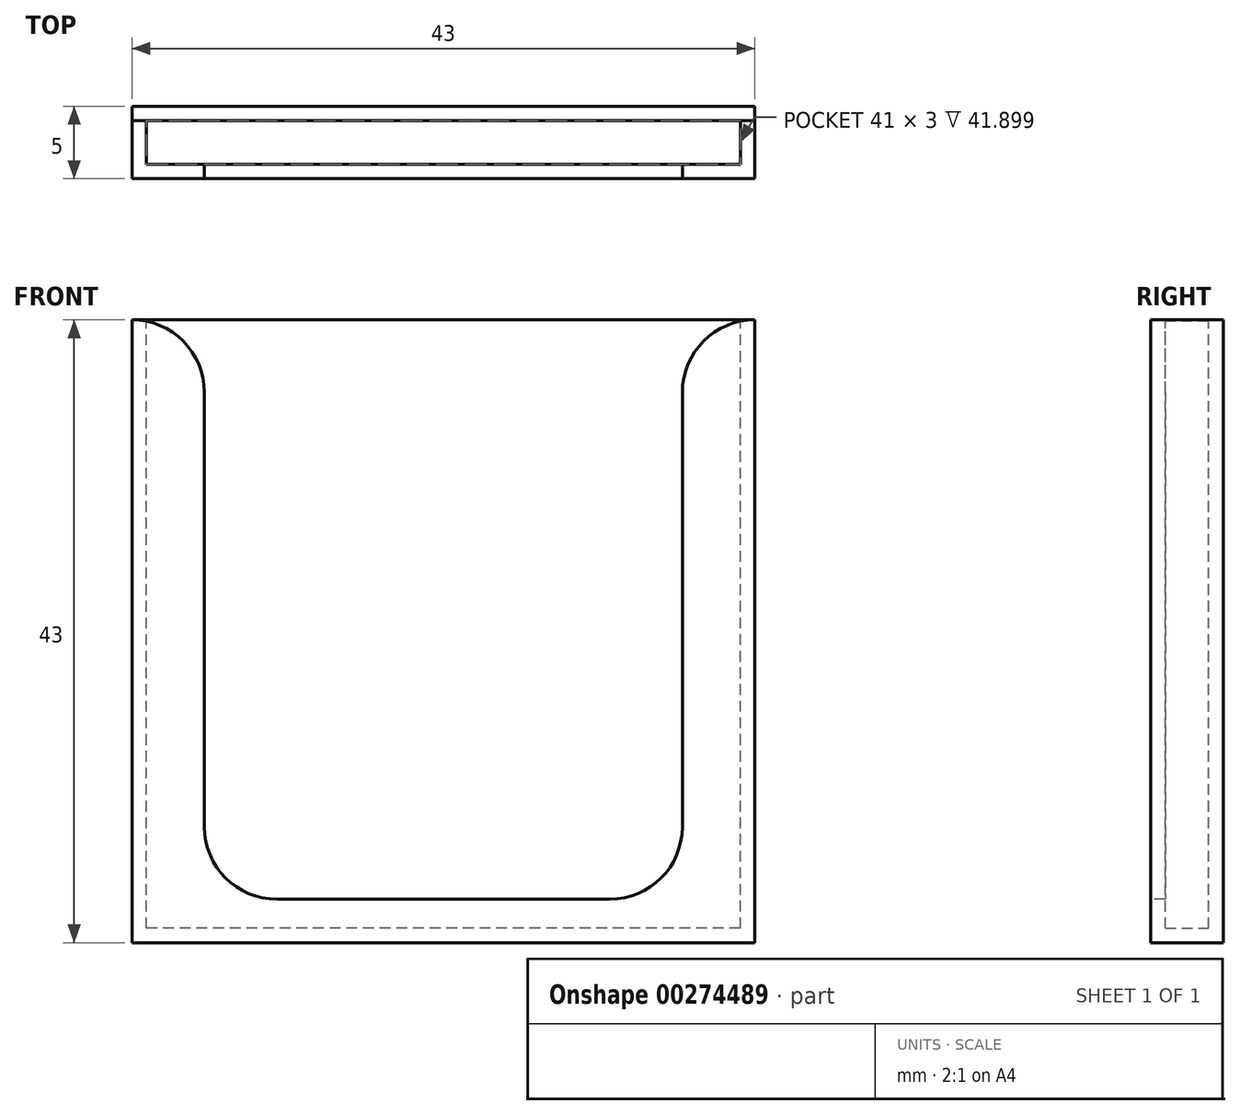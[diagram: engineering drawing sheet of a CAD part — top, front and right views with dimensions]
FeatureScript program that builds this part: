
annotation { "Feature Type Name" : "Feature", "Feature Type Description" : "" }
export const myFeature = defineFeature(function(context is Context, id is Id, definition is map)
    precondition{}
    {
        {
            var Q0;
            Q0=qCreatedBy(makeId("Front.planeOp"),FACE);
            var sketch = newSketch(context, id + "F0", { "sketchPlane" : qUnion([Q0])});
            skLineSegment(sketch, "E0.bottom", {"start": v(21.5, -21.5) * mm, "end": v(-21.5, -21.5) * mm});
            skLineSegment(sketch, "E0.top", {"start": v(21.5, 21.5) * mm, "end": v(-21.5, 21.5) * mm});
            skLineSegment(sketch, "E0.left", {"start": v(21.5, -21.5) * mm, "end": v(21.5, 21.5) * mm});
            skLineSegment(sketch, "E0.right", {"start": v(-21.5, -21.5) * mm, "end": v(-21.5, 21.5) * mm});
            skPoint(sketch, "E0.middle", {"position": v(0, 0) * mm});
            skSolve(sketch);
        }
        {
            var Q0;
            Q0=makeQuery(id+"F0.imprint","IMPRINT",FACE,{"disambiguationData":[TD([[makeQuery(id+"F0.imprint","IMPRINT",EDGE,{"derivedFrom":sQuery(id+"F0.wireOp",EDGE,"E0.bottom")}),-1.0]])]});
            extrude(context, id + "F1", {"entities" : qUnion([Q0]), "depth" : 5 * mm});
        }
        {
            var Q0;
            Q0=makeQuery(id+"F1.opExtrude","SWEPT_FACE",FACE,{"disambiguationData":[OSD([sQuery(id+"F0.wireOp",EDGE,"E0.top")])]});
            shell(context, id + "F2", {"entities" : qUnion([Q0]), "thickness" : 1 * mm});
        }
        {
            var Q0;
            Q0=makeQuery(id+"F1.opExtrude","CAP_FACE",FACE,{"disambiguationData":[OSD([sQuery(id+"F0.wireOp",EDGE,"E0.bottom"),sQuery(id+"F0.wireOp",EDGE,"E0.top"),sQuery(id+"F0.wireOp",EDGE,"E0.left"),sQuery(id+"F0.wireOp",EDGE,"E0.right")])],"isStart":false});
            var sketch = newSketch(context, id + "F3", { "sketchPlane" : qUnion([Q0])});
            skLineSegment(sketch, "E1.0", {"start": v(21.5, 21.5) * mm, "end": v(21.5, 21.5) * mm});
            skLineSegment(sketch, "E2", {"start": v(-16.5, 16.5) * mm, "end": v(-16.5, -13.5) * mm});
            skLineSegment(sketch, "E3", {"start": v(-11.5, -18.5) * mm, "end": v(11.5, -18.5) * mm});
            skLineSegment(sketch, "E4", {"start": v(16.5, -13.5) * mm, "end": v(16.5, 16.5) * mm});
            skLineSegment(sketch, "E5.trimOffspring", {"start": v(-21.5, 21.5) * mm, "end": v(-21.5, 21.5) * mm});
            skPoint(sketch, "E6.visualSharp", {"position": v(-16.5, 21.5) * mm});
            skArc(sketch, "E6.filletArc", {"start": v(-16.5, 16.5) * mm, "mid": v(-17.96, 20.04) * mm, "end": v(-21.5, 21.5) * mm});
            skPoint(sketch, "E7.visualSharp", {"position": v(16.5, 21.5) * mm});
            skArc(sketch, "E7.filletArc", {"start": v(21.5, 21.5) * mm, "mid": v(17.96, 20.04) * mm, "end": v(16.5, 16.5) * mm});
            skLineSegment(sketch, "E8", {"start": v(-21.5, 21.5) * mm, "end": v(21.5, 21.5) * mm});
            skPoint(sketch, "E9.visualSharp", {"position": v(-16.5, -18.5) * mm});
            skArc(sketch, "E9.filletArc", {"start": v(-16.5, -13.5) * mm, "mid": v(-15.04, -17.04) * mm, "end": v(-11.5, -18.5) * mm});
            skPoint(sketch, "E10.visualSharp", {"position": v(16.5, -18.5) * mm});
            skArc(sketch, "E10.filletArc", {"start": v(11.5, -18.5) * mm, "mid": v(15.04, -17.04) * mm, "end": v(16.5, -13.5) * mm});
            skSolve(sketch);
        }
        {
            var Q0;
            Q0=makeQuery(id+"F3.imprint","IMPRINT",FACE,{"disambiguationData":[TD([[makeQuery(id+"F3.imprint","IMPRINT",EDGE,{"derivedFrom":sQuery(id+"F3.wireOp",EDGE,"E2")}),1.0]])]});
            var Q1;
            {var subQ0=sQuery(id+"F0.wireOp",EDGE,"E0.right");var subQ1=sQuery(id+"F0.wireOp",EDGE,"E0.left");var subQ2=sQuery(id+"F0.wireOp",EDGE,"E0.top");var subQ3=sQuery(id+"F0.wireOp",EDGE,"E0.bottom");Q1=makeQuery(id+"F2.opShell","OFFSET_FACE",FACE,{"disambiguationData":[OSD([subQ3,subQ2,subQ1,subQ0]),TDD([makeQuery(id+"F1.opExtrude","CAP_FACE",FACE,{"disambiguationData":[OSD([subQ3,subQ2,subQ1,subQ0])],"isStart":true})])]});}
            extrude(context, id + "F4", {"entities" : qUnion([Q0]), "operationType" : NewBodyOperationType.REMOVE, "endBound" : BoundingType.UP_TO_SURFACE, "oppositeDirection" : true, "endBoundEntityFace" : qUnion([Q1]), "depth" : 25 * mm});
        }
    });
